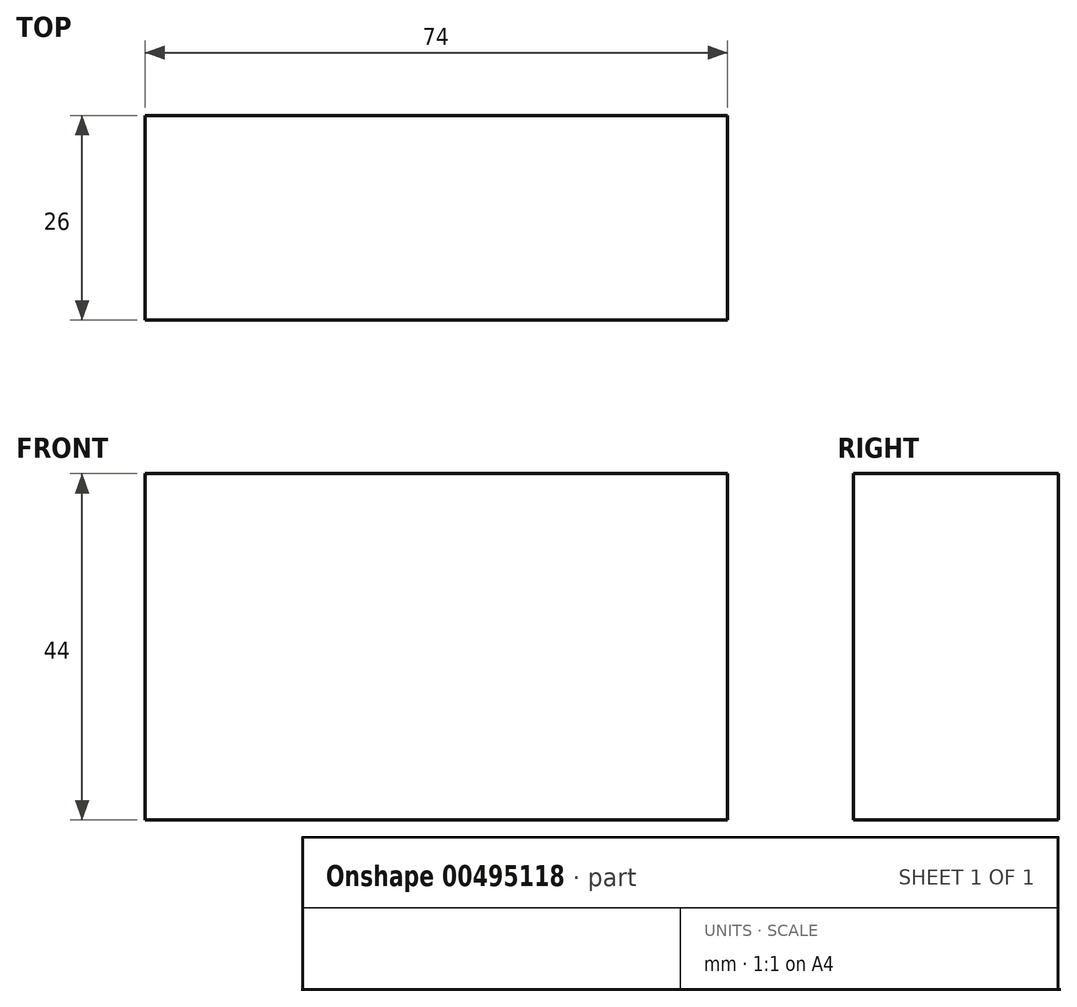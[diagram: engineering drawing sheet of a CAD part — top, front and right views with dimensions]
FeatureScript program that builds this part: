
annotation { "Feature Type Name" : "Feature", "Feature Type Description" : "" }
export const myFeature = defineFeature(function(context is Context, id is Id, definition is map)
    precondition{}
    {
        {
            var Q0;
            Q0=qCreatedBy(makeId("Front.planeOp"),FACE);
            var sketch = newSketch(context, id + "F0", { "sketchPlane" : qUnion([Q0])});
            skLineSegment(sketch, "E0.bottom", {"start": v(0, 0) * mm, "end": v(-74, 0) * mm});
            skLineSegment(sketch, "E0.top", {"start": v(0, 44) * mm, "end": v(-74, 44) * mm});
            skLineSegment(sketch, "E0.left", {"start": v(0, 0) * mm, "end": v(0, 44) * mm});
            skLineSegment(sketch, "E0.right", {"start": v(-74, 0) * mm, "end": v(-74, 44) * mm});
            skSolve(sketch);
        }
        {
            var Q0;
            Q0=makeQuery(id+"F0.imprint","IMPRINT",FACE,{"disambiguationData":[TD([[makeQuery(id+"F0.imprint","IMPRINT",EDGE,{"derivedFrom":sQuery(id+"F0.wireOp",EDGE,"E0.bottom")}),-1.0]])]});
            extrude(context, id + "F1", {"entities" : qUnion([Q0]), "depth" : 26 * mm});
        }
    });
